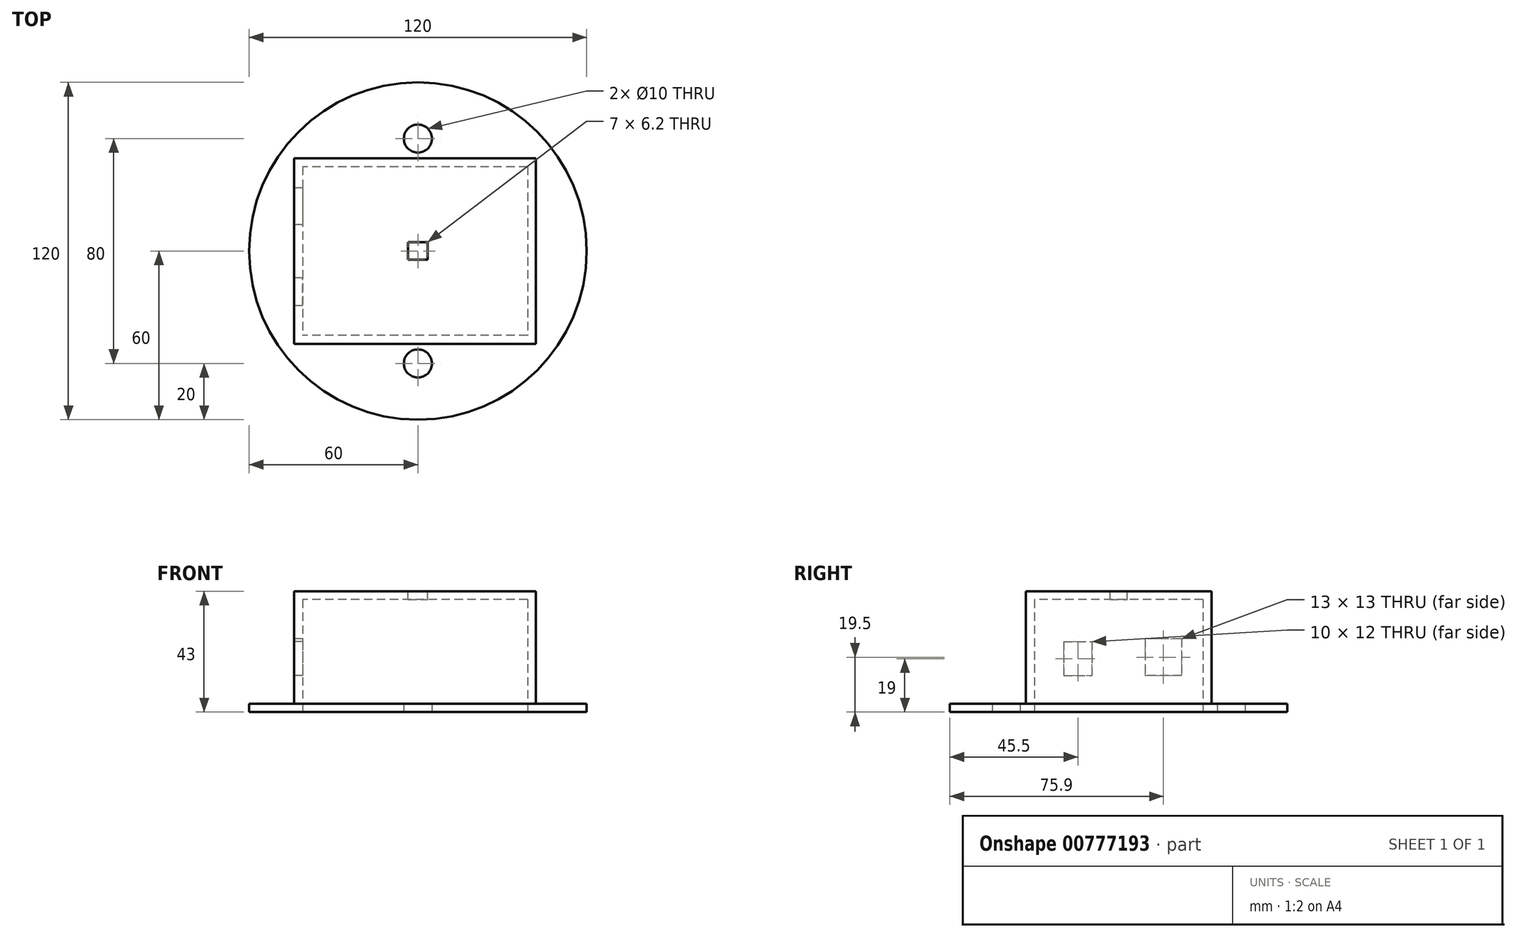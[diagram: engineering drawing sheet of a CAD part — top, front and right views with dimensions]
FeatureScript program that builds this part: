
annotation { "Feature Type Name" : "Feature", "Feature Type Description" : "" }
export const myFeature = defineFeature(function(context is Context, id is Id, definition is map)
    precondition{}
    {
        {
            var Q0;
            Q0=qCreatedBy(makeId("Top.planeOp"),FACE);
            var sketch = newSketch(context, id + "F0", { "sketchPlane" : qUnion([Q0])});
            skCircle(sketch, "E0", {"center": v(0, 0) * mm, "radius": 60 * mm});
            skCircle(sketch, "E1", {"center": v(0, 40) * mm, "radius": 5 * mm});
            skCircle(sketch, "E2", {"center": v(0, -40) * mm, "radius": 5 * mm});
            skLineSegment(sketch, "E3", {"start": v(39, 2) * mm, "end": v(39, 30) * mm});
            skLineSegment(sketch, "E4", {"start": v(-41, 0) * mm, "end": v(-41, -30) * mm});
            skLineSegment(sketch, "E5.bottom", {"start": v(39, 30) * mm, "end": v(-41, 30) * mm});
            skLineSegment(sketch, "E5.top", {"start": v(39, -30) * mm, "end": v(-41, -30) * mm});
            skLineSegment(sketch, "E5.left", {"start": v(39, 30) * mm, "end": v(39, -30) * mm});
            skLineSegment(sketch, "E5.right", {"start": v(-41, 30) * mm, "end": v(-41, -30) * mm});
            skLineSegment(sketch, "E6.0", {"start": v(-44, 33) * mm, "end": v(-44, -33) * mm});
            skLineSegment(sketch, "E6.1", {"start": v(42, 33) * mm, "end": v(-44, 33) * mm});
            skLineSegment(sketch, "E6.2", {"start": v(42, 33) * mm, "end": v(42, -33) * mm});
            skLineSegment(sketch, "E6.3", {"start": v(42, -33) * mm, "end": v(-44, -33) * mm});
            skSolve(sketch);
        }
        {
            var Q0;
            Q0=qSketchRegion(id+"F0",true);
            extrude(context, id + "F1", {"entities" : qUnion([Q0]), "depth" : 3 * mm, "offsetDistance" : 25 * mm});
        }
        {
            var Q0;
            {var subQ3=sQuery(id+"F0.wireOp",EDGE,"E5.bottom");Q0=makeQuery(id+"F0.imprint","IMPRINT",FACE,{"disambiguationData":[TD([[makeQuery(id+"F0.imprint","IMPRINT",EDGE,{"derivedFrom":subQ3}),-1.0]])]});}
            extrude(context, id + "F2", {"entities" : qUnion([Q0]), "operationType" : NewBodyOperationType.ADD, "depth" : 40 * mm, "offsetDistance" : 25 * mm});
        }
        {
            var Q0;
            Q0=makeQuery(id+"F2.opExtrude","CAP_FACE",FACE,{"disambiguationData":[OSD([sQuery(id+"F0.wireOp",EDGE,"E5.bottom"),sQuery(id+"F0.wireOp",EDGE,"E5.top"),sQuery(id+"F0.wireOp",EDGE,"E5.left"),sQuery(id+"F0.wireOp",EDGE,"E5.right"),sQuery(id+"F0.wireOp",EDGE,"E6.0"),sQuery(id+"F0.wireOp",EDGE,"E6.1"),sQuery(id+"F0.wireOp",EDGE,"E6.2"),sQuery(id+"F0.wireOp",EDGE,"E6.3")])],"isStart":false});
            var sketch = newSketch(context, id + "F3", { "sketchPlane" : qUnion([Q0])});
            skLineSegment(sketch, "E7.bottom", {"start": v(-44, 33) * mm, "end": v(42, 33) * mm});
            skLineSegment(sketch, "E7.top", {"start": v(-44, -33) * mm, "end": v(42, -33) * mm});
            skLineSegment(sketch, "E7.left", {"start": v(-44, 33) * mm, "end": v(-44, -33) * mm});
            skLineSegment(sketch, "E7.right", {"start": v(42, 33) * mm, "end": v(42, -33) * mm});
            skSolve(sketch);
        }
        {
            var Q0;
            Q0=qSketchRegion(id+"F3",true);
            extrude(context, id + "F4", {"entities" : qUnion([Q0]), "operationType" : NewBodyOperationType.ADD, "depth" : 3 * mm, "offsetDistance" : 25 * mm});
        }
        {
            var Q0;
            Q0=makeQuery(id+"F4.boolean.opBoolean","MERGE",FACE,{"derivedFrom":[makeQuery(id+"F2.opExtrude","SWEPT_FACE",FACE,{"disambiguationData":[OSD([sQuery(id+"F0.wireOp",EDGE,"E6.0")])]}),makeQuery(id+"F4.opExtrude","SWEPT_FACE",FACE,{"disambiguationData":[OSD([sQuery(id+"F3.wireOp",EDGE,"E7.left")])]})]});
            var sketch = newSketch(context, id + "F5", { "sketchPlane" : qUnion([Q0])});
            skLineSegment(sketch, "E8", {"start": v(0, 3) * mm, "end": v(0, 13) * mm});
            skLineSegment(sketch, "E9", {"start": v(0, 13) * mm, "end": v(9.5, 13) * mm});
            skLineSegment(sketch, "E10", {"start": v(0, 13) * mm, "end": v(-9.4, 13) * mm});
            skLineSegment(sketch, "E11.bottom", {"start": v(9.5, 13) * mm, "end": v(19.5, 13) * mm});
            skLineSegment(sketch, "E11.top", {"start": v(9.5, 25) * mm, "end": v(19.5, 25) * mm});
            skLineSegment(sketch, "E11.left", {"start": v(9.5, 13) * mm, "end": v(9.5, 25) * mm});
            skLineSegment(sketch, "E11.right", {"start": v(19.5, 13) * mm, "end": v(19.5, 25) * mm});
            skLineSegment(sketch, "E12.bottom", {"start": v(-9.4, 13) * mm, "end": v(-22.4, 13) * mm});
            skLineSegment(sketch, "E12.top", {"start": v(-9.4, 26) * mm, "end": v(-22.4, 26) * mm});
            skLineSegment(sketch, "E12.left", {"start": v(-9.4, 13) * mm, "end": v(-9.4, 26) * mm});
            skLineSegment(sketch, "E12.right", {"start": v(-22.4, 13) * mm, "end": v(-22.4, 26) * mm});
            skSolve(sketch);
        }
        {
            var Q0;
            Q0=qSketchRegion(id+"F5",true);
            extrude(context, id + "F6", {"entities" : qUnion([Q0]), "operationType" : NewBodyOperationType.REMOVE, "oppositeDirection" : true, "depth" : 25 * mm, "offsetDistance" : 25 * mm});
        }
        {
            var Q0;
            Q0=makeQuery(id+"F4.opExtrude","CAP_FACE",FACE,{"disambiguationData":[OSD([sQuery(id+"F3.wireOp",EDGE,"E7.bottom"),sQuery(id+"F3.wireOp",EDGE,"E7.top"),sQuery(id+"F3.wireOp",EDGE,"E7.left"),sQuery(id+"F3.wireOp",EDGE,"E7.right")])],"isStart":false});
            var sketch = newSketch(context, id + "F7", { "sketchPlane" : qUnion([Q0])});
            skLineSegment(sketch, "E13", {"start": v(3.5, 0) * mm, "end": v(3.5, 3.1) * mm});
            skLineSegment(sketch, "E14", {"start": v(-3.5, 0) * mm, "end": v(-3.5, -3.1) * mm});
            skLineSegment(sketch, "E15.bottom", {"start": v(-3.5, -3.1) * mm, "end": v(3.5, -3.1) * mm});
            skLineSegment(sketch, "E15.top", {"start": v(-3.5, 3.1) * mm, "end": v(3.5, 3.1) * mm});
            skLineSegment(sketch, "E15.left", {"start": v(-3.5, -3.1) * mm, "end": v(-3.5, 3.1) * mm});
            skLineSegment(sketch, "E15.right", {"start": v(3.5, -3.1) * mm, "end": v(3.5, 3.1) * mm});
            skSolve(sketch);
        }
        {
            var Q0;
            Q0=qSketchRegion(id+"F7",true);
            extrude(context, id + "F8", {"entities" : qUnion([Q0]), "operationType" : NewBodyOperationType.REMOVE, "oppositeDirection" : true, "depth" : 25 * mm, "offsetDistance" : 25 * mm});
        }
    });
